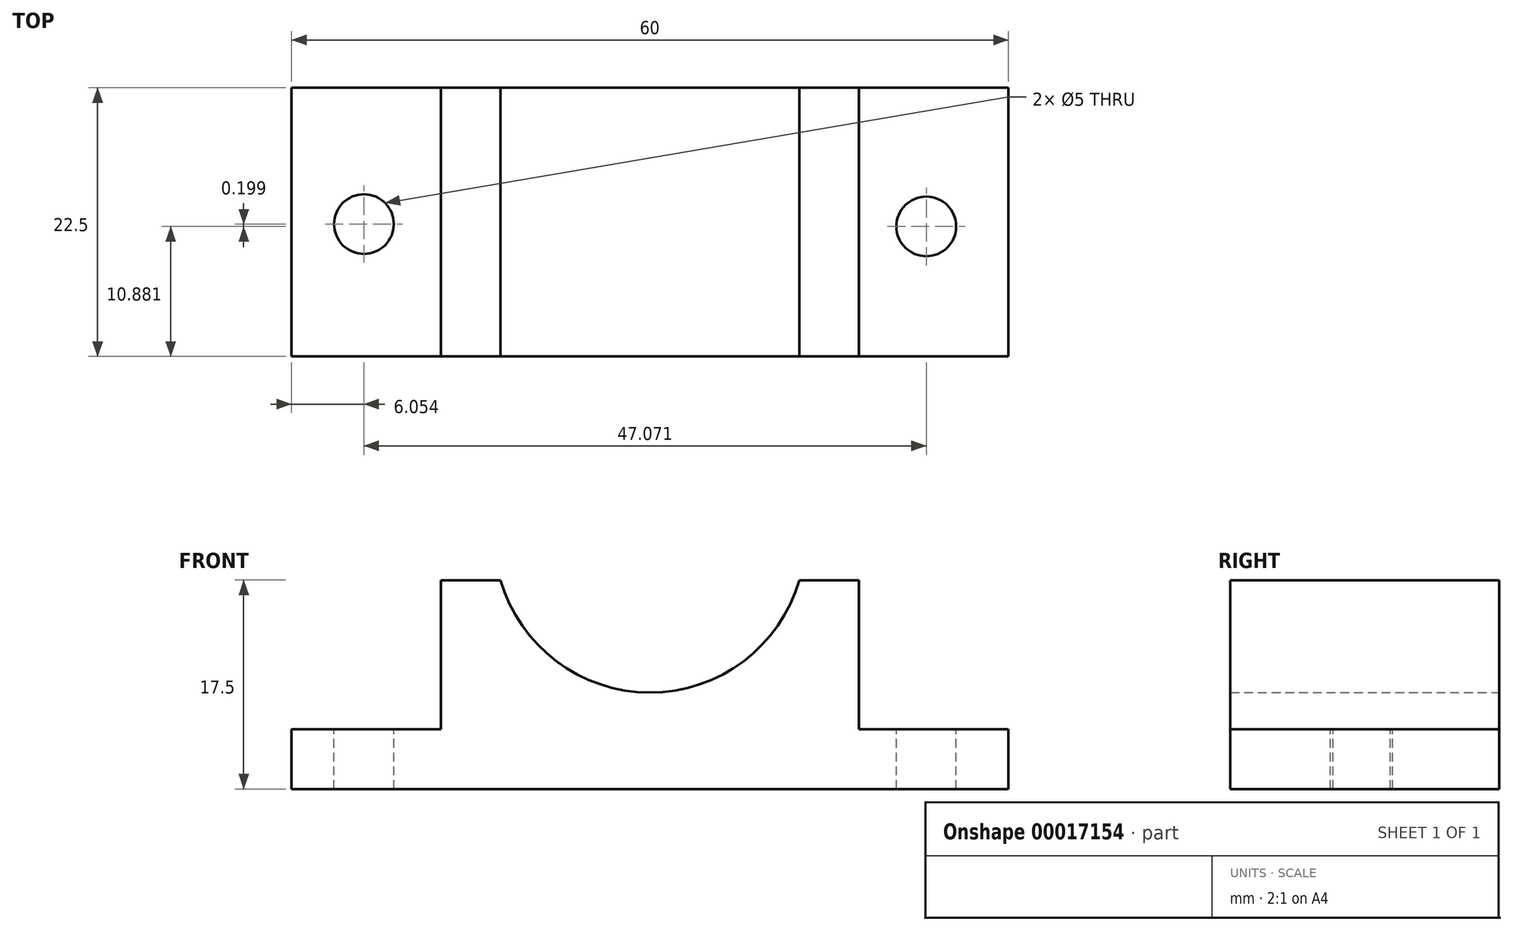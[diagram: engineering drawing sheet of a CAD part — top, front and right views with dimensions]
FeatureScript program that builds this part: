
annotation { "Feature Type Name" : "Feature", "Feature Type Description" : "" }
export const myFeature = defineFeature(function(context is Context, id is Id, definition is map)
    precondition{}
    {
        {
            var Q0;
            Q0=qCreatedBy(makeId("Front.planeOp"),FACE);
            var sketch = newSketch(context, id + "F0", { "sketchPlane" : qUnion([Q0])});
            skLineSegment(sketch, "E0", {"start": v(-29.5, -30.65) * mm, "end": v(30.5, -30.65) * mm});
            skLineSegment(sketch, "E1", {"start": v(30.5, -30.65) * mm, "end": v(30.5, -25.65) * mm});
            skLineSegment(sketch, "E2", {"start": v(30.5, -25.65) * mm, "end": v(18, -25.65) * mm});
            skLineSegment(sketch, "E3", {"start": v(-29.5, -30.65) * mm, "end": v(-29.5, -25.65) * mm});
            skLineSegment(sketch, "E4", {"start": v(-29.5, -25.65) * mm, "end": v(-17, -25.65) * mm});
            skLineSegment(sketch, "E5", {"start": v(-17, -25.65) * mm, "end": v(-17, -13.15) * mm});
            skLineSegment(sketch, "E6", {"start": v(-17, -13.15) * mm, "end": v(-12, -13.15) * mm});
            skLineSegment(sketch, "E7", {"start": v(18, -25.65) * mm, "end": v(18, -13.15) * mm});
            skLineSegment(sketch, "E8", {"start": v(18, -13.15) * mm, "end": v(13, -13.15) * mm});
            skArc(sketch, "E9", {"start": v(-12, -13.15) * mm, "mid": v(0.5, -22.57) * mm, "end": v(13, -13.15) * mm});
            skSolve(sketch);
        }
        {
            var Q0;
            Q0 = qSketchRegion(id + "F0", true);
            extrude(context, id + "F1", {"entities" : qUnion([Q0]), "depth" : 22.5 * mm});
        }
        {
            var Q0;
            Q0=makeQuery(id+"F1.opExtrude","SWEPT_FACE",FACE,{"disambiguationData":[OSD([sQuery(id+"F0.wireOp",EDGE,"E4")])]});
            var sketch = newSketch(context, id + "F2", { "sketchPlane" : qUnion([Q0])});
            skCircle(sketch, "E10", {"center": v(-23.44, -11.42) * mm, "radius": 2.5 * mm});
            skCircle(sketch, "E11", {"center": v(23.63, -11.62) * mm, "radius": 2.5 * mm});
            skSolve(sketch);
        }
        {
            var Q0;
            Q0 = qSketchRegion(id + "F2", true);
            extrude(context, id + "F3", {"entities" : qUnion([Q0]), "operationType" : NewBodyOperationType.REMOVE, "endBound" : BoundingType.THROUGH_ALL, "oppositeDirection" : true, "depth" : 25 * mm});
        }
    });
